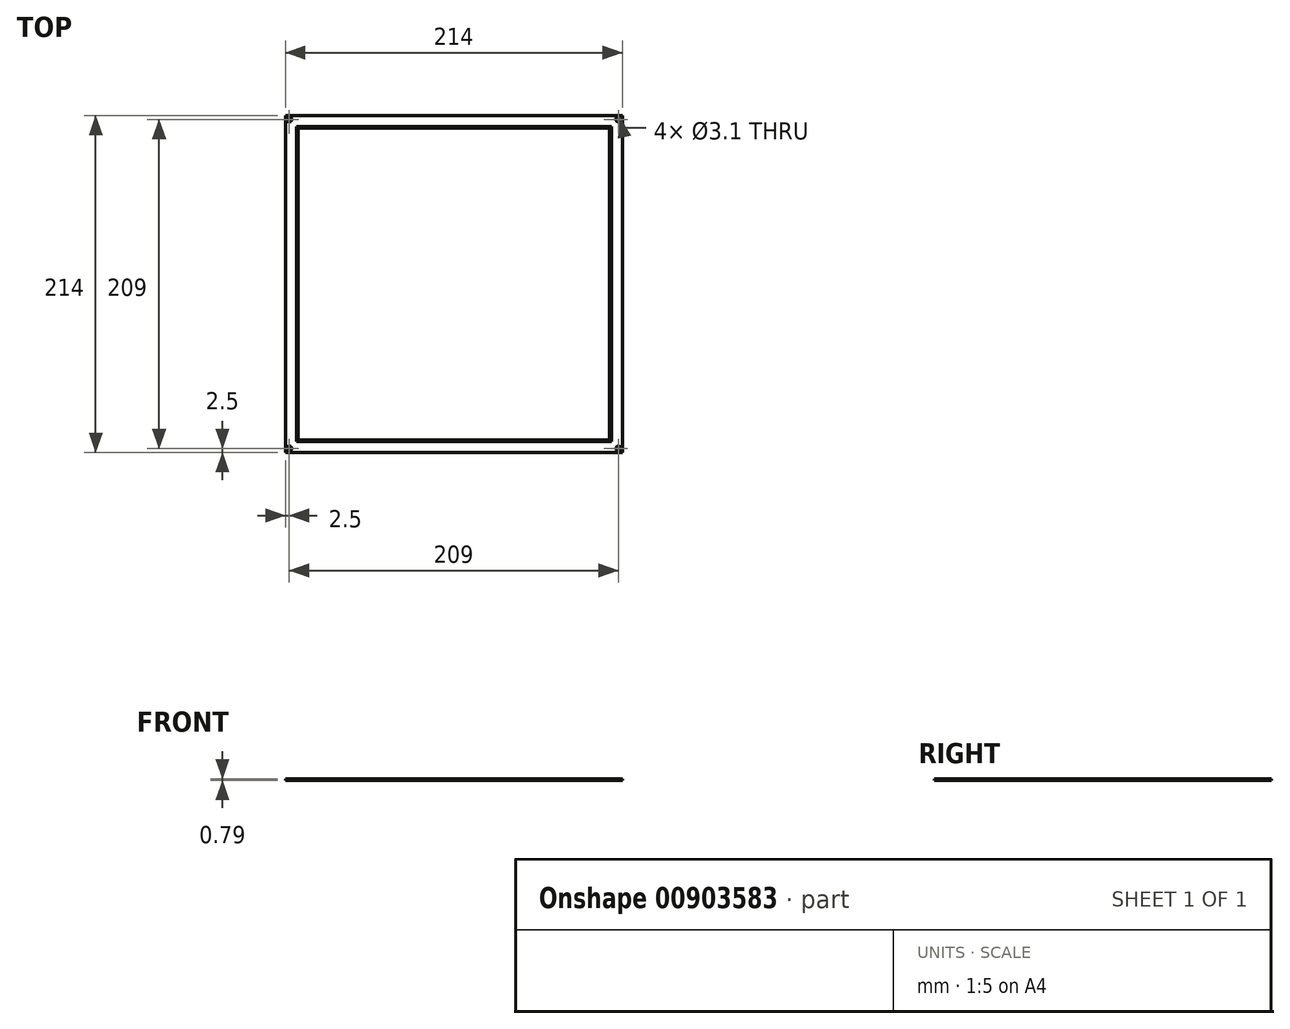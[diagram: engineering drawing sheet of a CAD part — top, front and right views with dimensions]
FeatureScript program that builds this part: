
annotation { "Feature Type Name" : "Feature", "Feature Type Description" : "" }
export const myFeature = defineFeature(function(context is Context, id is Id, definition is map)
    precondition{}
    {
        {
            var Q0;
            Q0=qCreatedBy(makeId("Top.planeOp"),FACE);
            var sketch = newSketch(context, id + "F0", { "sketchPlane" : qUnion([Q0])});
            skLineSegment(sketch, "E0.bottom", {"start": v(-107, 107) * mm, "end": v(107, 107) * mm});
            skLineSegment(sketch, "E0.top", {"start": v(-107, -107) * mm, "end": v(107, -107) * mm});
            skLineSegment(sketch, "E0.left", {"start": v(-107, 107) * mm, "end": v(-107, -107) * mm});
            skLineSegment(sketch, "E0.right", {"start": v(107, 107) * mm, "end": v(107, -107) * mm});
            skLineSegment(sketch, "E1", {"start": v(-107, 107) * mm, "end": v(107, -107) * mm, "construction": true});
            skLineSegment(sketch, "E2", {"start": v(107, 107) * mm, "end": v(-107, -107) * mm, "construction": true});
            skLineSegment(sketch, "E3.bottom", {"start": v(-104.5, 104.5) * mm, "end": v(104.5, 104.5) * mm, "construction": true});
            skLineSegment(sketch, "E3.top", {"start": v(-104.5, -104.5) * mm, "end": v(104.5, -104.5) * mm, "construction": true});
            skLineSegment(sketch, "E3.left", {"start": v(-104.5, 104.5) * mm, "end": v(-104.5, -104.5) * mm, "construction": true});
            skLineSegment(sketch, "E3.right", {"start": v(104.5, 104.5) * mm, "end": v(104.5, -104.5) * mm, "construction": true});
            skCircle(sketch, "E4", {"center": v(-104.5, 104.5) * mm, "radius": 1.55 * mm});
            skCircle(sketch, "E5", {"center": v(104.5, 104.5) * mm, "radius": 1.55 * mm});
            skCircle(sketch, "E6", {"center": v(104.5, -104.5) * mm, "radius": 1.55 * mm});
            skCircle(sketch, "E7", {"center": v(-104.5, -104.5) * mm, "radius": 1.55 * mm});
            skPoint(sketch, "E8", {"position": v(0, 0) * mm});
            skSolve(sketch);
        }
        {
            var Q0;
            Q0=makeQuery(id+"F0.imprint","IMPRINT",FACE,{"disambiguationData":[TD([[makeQuery(id+"F0.imprint","IMPRINT",EDGE,{"derivedFrom":sQuery(id+"F0.wireOp",EDGE,"E0.bottom")}),-1.0]])]});
            extrude(context, id + "F1", {"entities" : qUnion([Q0]), "depth" : 0.8 * mm});
        }
        {
            var Q0;
            Q0=makeQuery(id+"F1.opExtrude","CAP_FACE",FACE,{"disambiguationData":[OSD([sQuery(id+"F0.wireOp",EDGE,"E0.bottom"),sQuery(id+"F0.wireOp",EDGE,"E0.top"),sQuery(id+"F0.wireOp",EDGE,"E0.left"),sQuery(id+"F0.wireOp",EDGE,"E0.right"),sQuery(id+"F0.wireOp",EDGE,"E4"),sQuery(id+"F0.wireOp",EDGE,"E5"),sQuery(id+"F0.wireOp",EDGE,"E6"),sQuery(id+"F0.wireOp",EDGE,"E7")])],"isStart":false});
            var sketch = newSketch(context, id + "F2", { "sketchPlane" : qUnion([Q0])});
            skLineSegment(sketch, "E9.bottom", {"start": v(100, 100) * mm, "end": v(-100, 100) * mm});
            skLineSegment(sketch, "E9.top", {"start": v(100, -100) * mm, "end": v(-100, -100) * mm});
            skLineSegment(sketch, "E9.left", {"start": v(100, 100) * mm, "end": v(100, -100) * mm});
            skLineSegment(sketch, "E9.right", {"start": v(-100, 100) * mm, "end": v(-100, -100) * mm});
            skPoint(sketch, "E9.middle", {"position": v(0, 0) * mm});
            skLineSegment(sketch, "E10.0", {"start": v(99, 99) * mm, "end": v(-99, 99) * mm});
            skLineSegment(sketch, "E10.1", {"start": v(99, 99) * mm, "end": v(99, -99) * mm});
            skLineSegment(sketch, "E10.2", {"start": v(99, -99) * mm, "end": v(-99, -99) * mm});
            skLineSegment(sketch, "E10.3", {"start": v(-99, 99) * mm, "end": v(-99, -99) * mm});
            skSolve(sketch);
        }
        {
            var Q0;
            Q0=qSketchRegion(id+"F2",true);
            extrude(context, id + "F3", {"entities" : qUnion([Q0]), "operationType" : NewBodyOperationType.REMOVE, "endBound" : BoundingType.SYMMETRIC, "depth" : .5 * mm});
        }
    });
